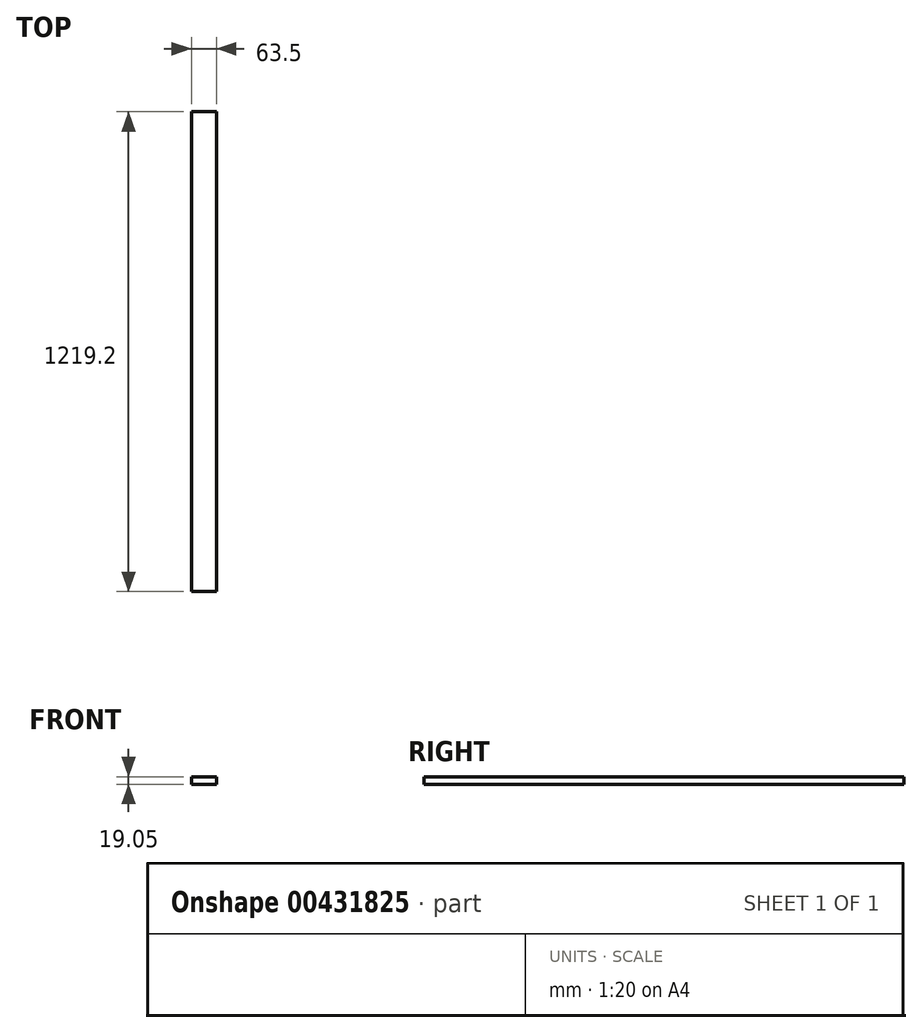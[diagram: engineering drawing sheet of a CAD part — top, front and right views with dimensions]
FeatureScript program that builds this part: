
annotation { "Feature Type Name" : "Feature", "Feature Type Description" : "" }
export const myFeature = defineFeature(function(context is Context, id is Id, definition is map)
    precondition{}
    {
        {
            var Q0;
            Q0=qCreatedBy(makeId("Top.planeOp"),FACE);
            var sketch = newSketch(context, id + "F0", { "sketchPlane" : qUnion([Q0])});
            skLineSegment(sketch, "E0.bottom", {"start": v(31.75, 609.6) * mm, "end": v(-31.75, 609.6) * mm});
            skLineSegment(sketch, "E0.top", {"start": v(31.75, -609.6) * mm, "end": v(-31.75, -609.6) * mm});
            skLineSegment(sketch, "E0.left", {"start": v(31.75, 609.6) * mm, "end": v(31.75, -609.6) * mm});
            skLineSegment(sketch, "E0.right", {"start": v(-31.75, 609.6) * mm, "end": v(-31.75, -609.6) * mm});
            skPoint(sketch, "E0.middle", {"position": v(0, 0) * mm});
            skSolve(sketch);
        }
        {
            var Q0;
            Q0=makeQuery(id+"F0.imprint","IMPRINT",FACE,{"disambiguationData":[TD([[makeQuery(id+"F0.imprint","IMPRINT",EDGE,{"derivedFrom":sQuery(id+"F0.wireOp",EDGE,"E0.bottom")}),1.0]])]});
            extrude(context, id + "F1", {"entities" : qUnion([Q0]), "depth" : 19.05 * mm});
        }
    });
